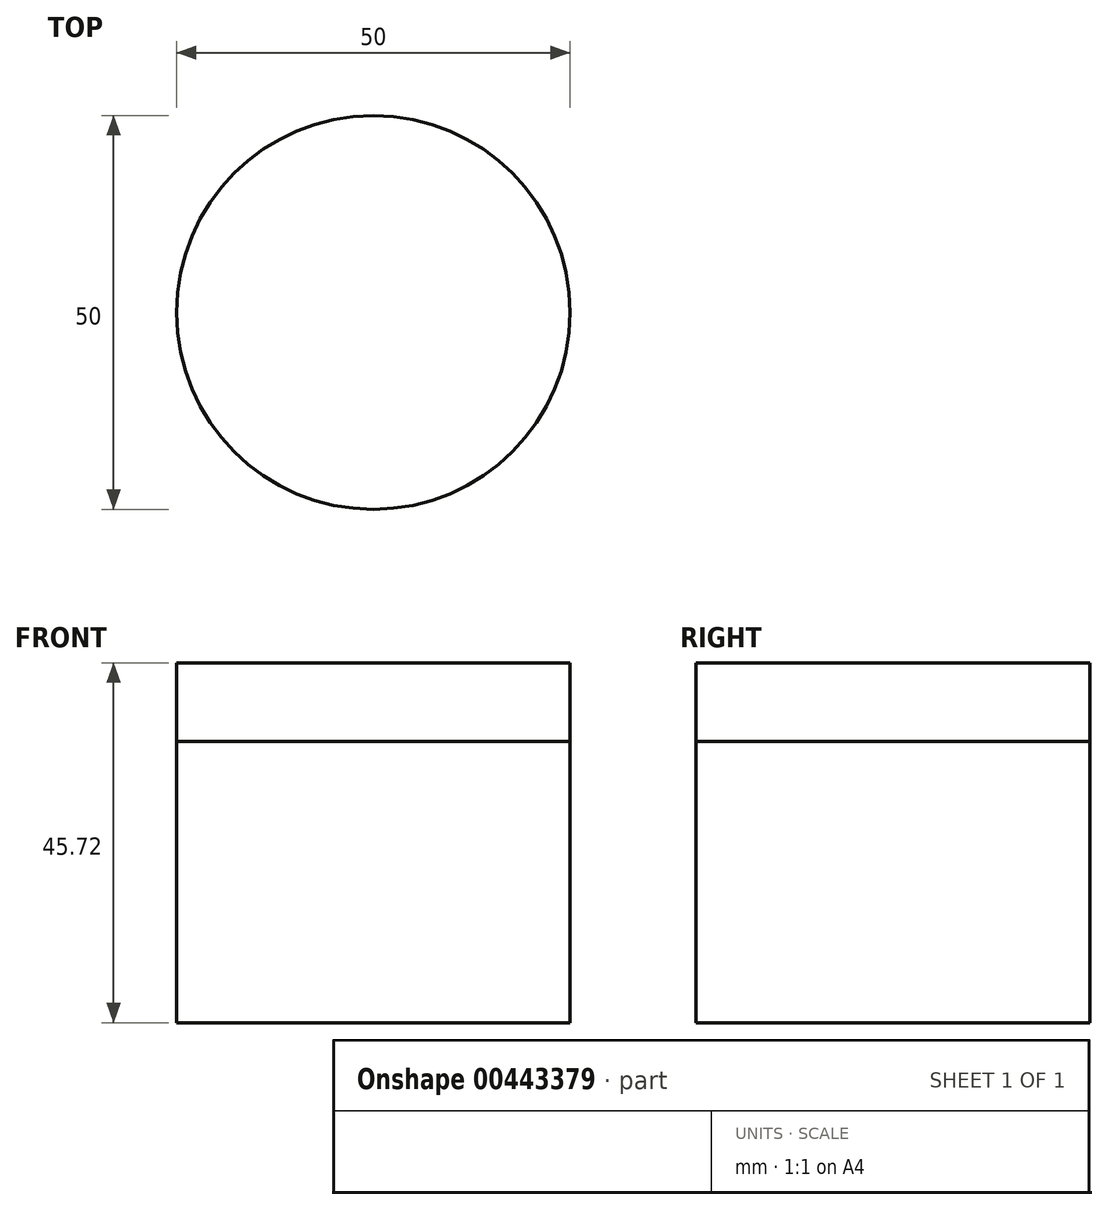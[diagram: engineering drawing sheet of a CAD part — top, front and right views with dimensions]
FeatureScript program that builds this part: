
annotation { "Feature Type Name" : "Feature", "Feature Type Description" : "" }
export const myFeature = defineFeature(function(context is Context, id is Id, definition is map)
    precondition{}
    {
        {
            var Q0;
            Q0=qCreatedBy(makeId("Top.planeOp"),FACE);
            var sketch = newSketch(context, id + "F0", { "sketchPlane" : qUnion([Q0])});
            skCircle(sketch, "E0", {"center": v(0, 0) * mm, "radius": 25 * mm});
            skCircle(sketch, "E1", {"center": v(0, 0) * mm, "radius": 21 * mm});
            skSolve(sketch);
        }
        {
            var Q0;
            Q0 = qSketchRegion(id + "F0", true);
            var Q1;
            Q1=makeQuery(id+"F0.imprint","IMPRINT",FACE,{"disambiguationData":[TD([[makeQuery(id+"F0.imprint","IMPRINT",EDGE,{"derivedFrom":sQuery(id+"F0.wireOp",EDGE,"E1")}),1.0]])]});
            extrude(context, id + "F1", {"entities" : qUnion([Q0, Q1]), "oppositeDirection" : true, "depth" : 10 * mm});
        }
        {
            var Q0;
            Q0=qCreatedBy(makeId("Top.planeOp"),FACE);
            var sketch = newSketch(context, id + "F2", { "sketchPlane" : qUnion([Q0])});
            skCircle(sketch, "E2", {"center": v(0, 0) * mm, "radius": 25 * mm});
            skSolve(sketch);
        }
        {
            var Q0;
            Q0 = qSketchRegion(id + "F2", true);
            extrude(context, id + "F3", {"entities" : qUnion([Q0]), "oppositeDirection" : true, "depth" : 45.72 * mm});
        }
    });
